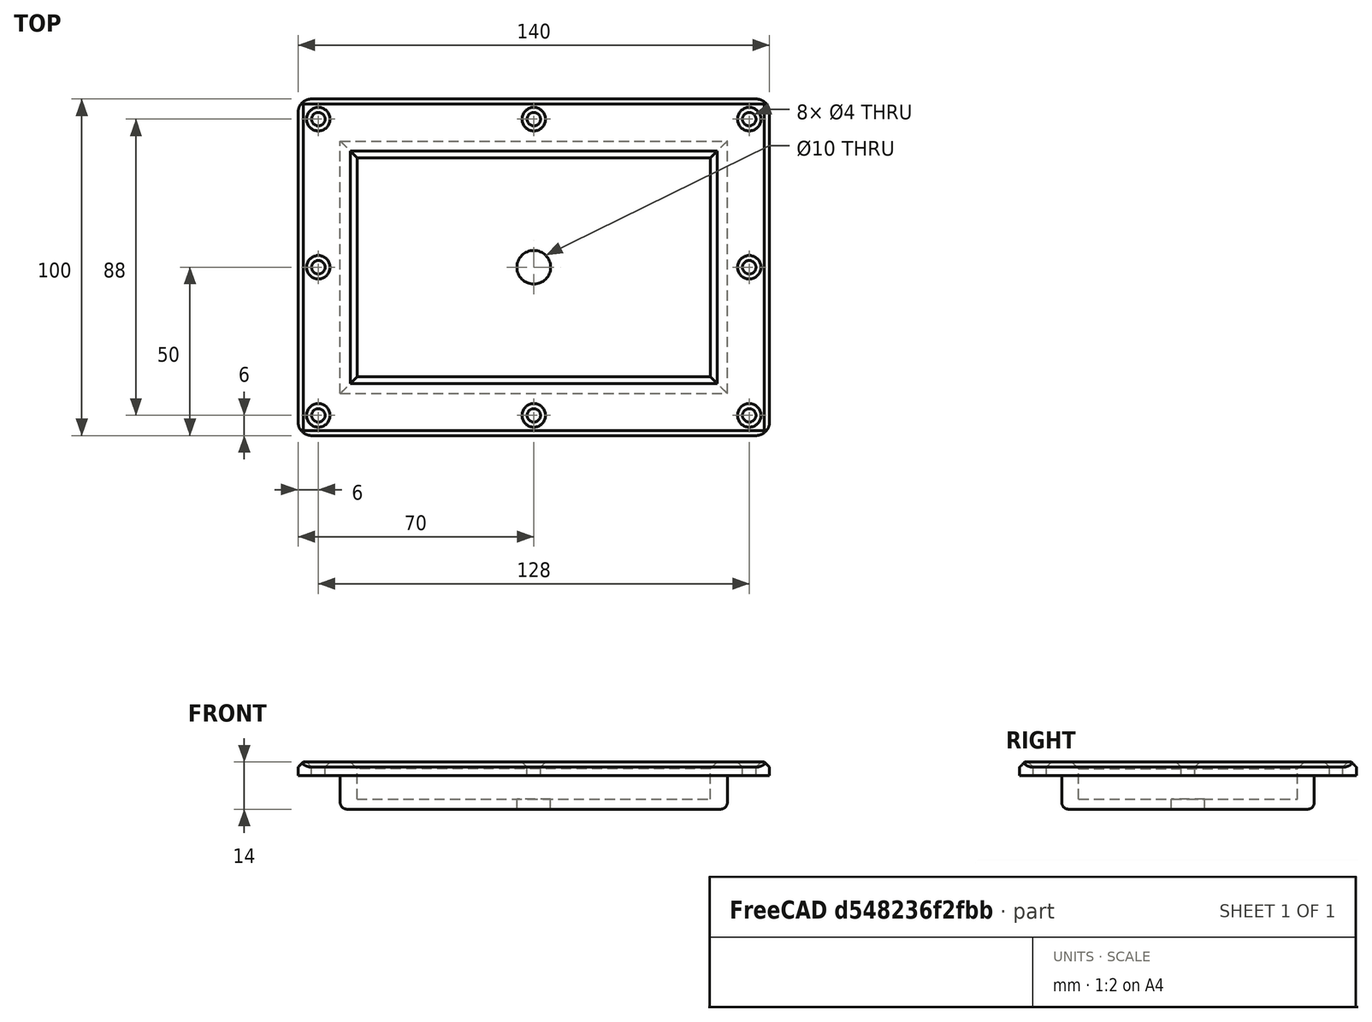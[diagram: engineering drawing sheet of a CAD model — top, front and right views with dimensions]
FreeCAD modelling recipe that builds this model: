
FCSTD DOCUMENT  (FreeCAD 0.15R4671 (Git))
Label: floor-monitor-plate2
License: All rights reserved
LicenseURL: http://en.wikipedia.org/wiki/All_rights_reserved
objects: Part::Cut×10, Part::Cylinder×9, Part::Box×3, Part::Fillet×3, PartDesign::Chamfer×2, Part::Fuse×1, Part::Chamfer×1, Drawing::FeatureViewPart×1, Drawing::FeaturePage×1
note: 29 computed .brp shape members not serialized (recipe doc carries the construction recipe); baked Part::Feature solids carry a one-line shape summary decoded from their .brp

FEATURE [Part::Box] Box  label="Cube"
  Height = 4
  Length = 140
  Width = 100
FEATURE [Part::Cylinder] Cylinder
  Angle = 360
  Height = 10
  Placement = pos=(134,6,0) rot=(0,0,1;0rad)
  Radius = 2
FEATURE [Part::Cylinder] Cylinder001
  Angle = 360
  Height = 10
  Placement = pos=(134,50,0) rot=(0,0,1;0rad)
  Radius = 2
FEATURE [Part::Cylinder] Cylinder002
  Angle = 360
  Height = 10
  Placement = pos=(6,50,0) rot=(0,0,1;0rad)
  Radius = 2
FEATURE [Part::Cylinder] Cylinder003
  Angle = 360
  Height = 10
  Placement = pos=(6,94,0) rot=(0,0,1;0rad)
  Radius = 2
FEATURE [Part::Cylinder] Cylinder004
  Angle = 360
  Height = 10
  Placement = pos=(6,6,0) rot=(0,0,1;0rad)
  Radius = 2
FEATURE [Part::Cylinder] Cylinder005
  Angle = 360
  Height = 10
  Placement = pos=(134,94,0) rot=(0,0,1;0rad)
  Radius = 2
FEATURE [Part::Cut] Cut
  Base = -> Box
  Tool = -> Cylinder
FEATURE [Part::Cut] Cut001
  Base = -> Cut
  Tool = -> Cylinder001
FEATURE [Part::Cut] Cut002
  Base = -> Cut001
  Tool = -> Cylinder005
FEATURE [Part::Cut] Cut003
  Base = -> Cut002
  Tool = -> Cylinder004
FEATURE [Part::Cut] Cut004
  Base = -> Cut003
  Tool = -> Cylinder002
FEATURE [Part::Cut] Cut005
  Base = -> Cut004
  Placement = pos=(0,0,10) rot=(0,0,1;0rad)
  Tool = -> Cylinder003
FEATURE [PartDesign::Chamfer] Chamfer
  Base = -> Cut005 [Edge11,Edge14,Edge2,Edge8,Edge7,Edge9,Edge10,Edge12,Edge13,Edge15]
  Placement = pos=(0,0,10) rot=(0,0,1;0rad)
  Size = 1.5
FEATURE [Part::Cylinder] Cylinder006
  Angle = 360
  Height = 20
  Placement = pos=(70,50,-5) rot=(0,0,1;0rad)
  Radius = 5
FEATURE [Part::Box] Box001  label="Cube001"
  Height = 10
  Length = 115
  Placement = pos=(12.5,12.5,0) rot=(0,0,1;0rad)
  Width = 75
FEATURE [Part::Fillet] Fillet
  Base = -> Box001
  Edges = 4 edges r=2: [Edge4,Edge8,Edge9,Edge11]
FEATURE [Part::Box] Box002  label="Cube002"
  Height = 20
  Length = 105
  Placement = pos=(17.5,17.5,3) rot=(0,0,1;0rad)
  Width = 65
FEATURE [Part::Fuse] Fusion
  Base = -> Chamfer
  Tool = -> Fillet
FEATURE [Part::Cut] Cut006
  Base = -> Fusion
  Tool = -> Box002
FEATURE [Part::Cut] Cut007
  Base = -> Cut006
  Tool = -> Cylinder006
FEATURE [PartDesign::Chamfer] Chamfer001
  Base = -> Cut007 [Edge30,Edge33,Edge32,Edge31]
  Size = 2
FEATURE [Part::Fillet] Fillet001
  Base = -> Chamfer001
  Edges = 2 edges r=4: [Edge54,Edge56]
FEATURE [Part::Fillet] Fillet002
  Base = -> Fillet001
  Edges = 2 edges r=4: [Edge7,Edge31]
FEATURE [Part::Cylinder] Cylinder007
  Angle = 360
  Height = 20
  Placement = pos=(70,94,0) rot=(0,0,1;0rad)
  Radius = 2
FEATURE [Part::Cut] Cut008
  Base = -> Fillet002
  Tool = -> Cylinder007
FEATURE [Part::Cylinder] Cylinder008
  Angle = 360
  Height = 20
  Placement = pos=(70,6,0) rot=(0,0,1;0rad)
  Radius = 2
FEATURE [Part::Cut] Cut009
  Base = -> Cut008
  Tool = -> Cylinder008
FEATURE [Part::Chamfer] Chamfer002
  Base = -> Cut009
  Edges = 2 edges r=1.5: [Edge27,Edge29]
FEATURE [Drawing::FeatureViewPart] View001
  Direction = (0,0,1)
  HiddenWidth = 0.15
  LineWidth = 0.35
  Rotation = 0
  ShowHiddenLines = false
  ShowSmoothLines = false
  Source = -> Chamfer002
  Tolerance = 0.05
  ViewResult = <blob: 4398 chars omitted>
  Visible = true
  X = 50
  Y = 130
FEATURE [Drawing::FeaturePage] Page
  EditableTexts = Designed by Name | Date | Scale | Weight | Title | Subtitle | Drawing number | Sheet
  Group = -> [View001]
  Template = D:/Program Files/FreeCAD 0.15/data/Mod/Drawing/Templates/A4_Landscape.svg
